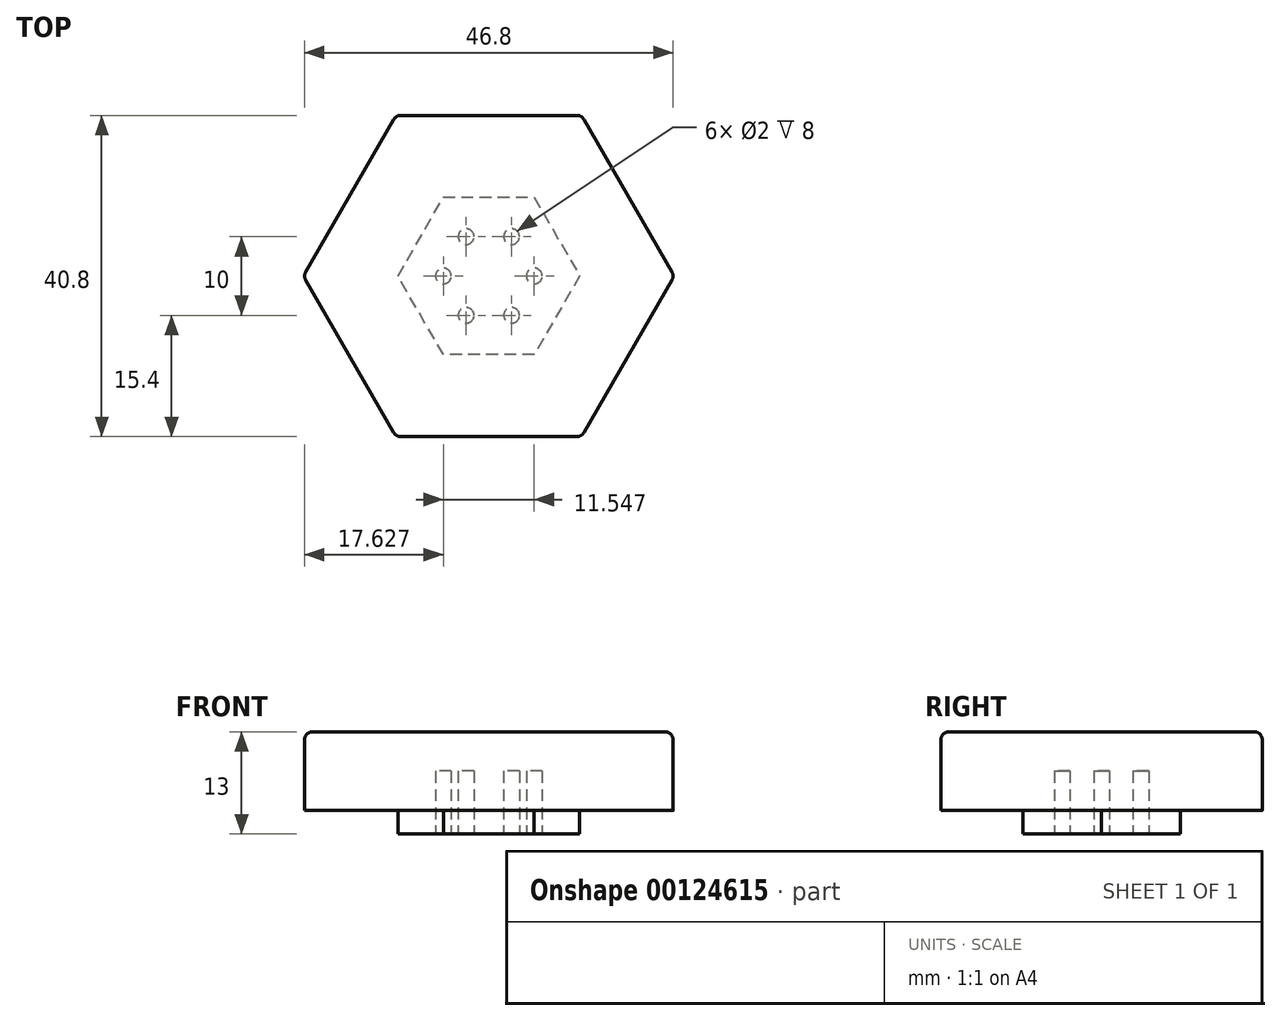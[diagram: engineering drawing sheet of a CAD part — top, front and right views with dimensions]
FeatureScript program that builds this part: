
annotation { "Feature Type Name" : "Feature", "Feature Type Description" : "" }
export const myFeature = defineFeature(function(context is Context, id is Id, definition is map)
    precondition{}
    {
        {
            var Q0;
            Q0=qCreatedBy(makeId("Top.planeOp"),FACE);
            var sketch = newSketch(context, id + "F0", { "sketchPlane" : qUnion([Q0])});
            skCircle(sketch, "E0.cCircle", {"center": v(0, 0) * mm, "radius": 10 * mm, "construction": true});
            skLineSegment(sketch, "E0.0", {"start": v(-5.77, 10) * mm, "end": v(5.77, 10) * mm});
            skLineSegment(sketch, "E0.1", {"start": v(5.77, 10) * mm, "end": v(11.55, 0) * mm});
            skLineSegment(sketch, "E0.2", {"start": v(11.55, 0) * mm, "end": v(5.77, -10) * mm});
            skLineSegment(sketch, "E0.3", {"start": v(5.77, -10) * mm, "end": v(-5.77, -10) * mm});
            skLineSegment(sketch, "E0.4", {"start": v(-5.77, -10) * mm, "end": v(-11.55, 0) * mm});
            skLineSegment(sketch, "E0.5", {"start": v(-11.55, 0) * mm, "end": v(-5.77, 10) * mm});
            skPoint(sketch, "E0.0.midPoint", {"position": v(0, 10) * mm});
            skLineSegment(sketch, "E1.0", {"start": v(-2.89, 5) * mm, "end": v(2.89, 5) * mm});
            skLineSegment(sketch, "E1.1", {"start": v(5.77, 0) * mm, "end": v(2.89, -5) * mm});
            skLineSegment(sketch, "E1.2", {"start": v(2.89, -5) * mm, "end": v(-2.89, -5) * mm});
            skLineSegment(sketch, "E1.3", {"start": v(2.89, 5) * mm, "end": v(5.77, 0) * mm});
            skLineSegment(sketch, "E1.4", {"start": v(-2.89, -5) * mm, "end": v(-5.77, 0) * mm});
            skLineSegment(sketch, "E1.5", {"start": v(-5.77, 0) * mm, "end": v(-2.89, 5) * mm});
            skCircle(sketch, "E2", {"center": v(2.89, 5) * mm, "radius": 1 * mm});
            skCircle(sketch, "E3.1.0", {"center": v(-2.89, 5) * mm, "radius": 1 * mm});
            skCircle(sketch, "E3.2.0", {"center": v(-5.77, 0) * mm, "radius": 1 * mm});
            skCircle(sketch, "E3.3.0", {"center": v(-2.89, -5) * mm, "radius": 1 * mm});
            skCircle(sketch, "E3.4.0", {"center": v(2.89, -5) * mm, "radius": 1 * mm});
            skCircle(sketch, "E3.5.0", {"center": v(5.77, 0) * mm, "radius": 1 * mm});
            skSolve(sketch);
        }
        {
            var Q0;
            Q0=makeQuery(id+"F0.imprint","IMPRINT",FACE,{"disambiguationData":[TD([[makeQuery(id+"F0.imprint","IMPRINT",EDGE,{"derivedFrom":sQuery(id+"F0.wireOp",EDGE,"E0.0")}),-1.0]])]});
            var Q1;
            Q1=makeQuery(id+"F0.imprint","IMPRINT",FACE,{"disambiguationData":[TD([[makeQuery(id+"F0.imprint","IMPRINT",EDGE,{"derivedFrom":sQuery(id+"F0.wireOp",EDGE,"E0.0")}),-1.0]])]});
            var Q2;
            {var subQ5=sQuery(id+"F0.wireOp",EDGE,"E3.1.0");var subQ6=sQuery(id+"F0.wireOp",EDGE,"E1.0");var subQ7=makeQuery(id+"F0.imprint","INTERSECT",VERTEX,{"derivedFrom":[subQ6,subQ5]});Q2=makeQuery(id+"F0.imprint","IMPRINT",FACE,{"disambiguationData":[TD([[makeQuery(id+"F0.imprint","IMPRINT",EDGE,{"disambiguationData":[TD([[subQ7,-1.0]])],"derivedFrom":subQ6}),-1.0]])]});}
            extrude(context, id + "F1", {"entities" : qUnion([Q0, Q1, Q2]), "depth" : 3 * mm});
        }
        {
            var Q0;
            Q0=makeQuery(id+"F1.opExtrude","CAP_FACE",FACE,{"disambiguationData":[OSD([sQuery(id+"F0.wireOp",EDGE,"E0.0"),sQuery(id+"F0.wireOp",EDGE,"E0.1"),sQuery(id+"F0.wireOp",EDGE,"E0.2"),sQuery(id+"F0.wireOp",EDGE,"E0.3"),sQuery(id+"F0.wireOp",EDGE,"E0.4"),sQuery(id+"F0.wireOp",EDGE,"E0.5")])],"isStart":false});
            var sketch = newSketch(context, id + "F2", { "sketchPlane" : qUnion([Q0])});
            skCircle(sketch, "E4.cCircle", {"center": v(0, 0) * mm, "radius": 20.4 * mm, "construction": true});
            skLineSegment(sketch, "E4.0", {"start": v(-11.78, 20.4) * mm, "end": v(11.78, 20.4) * mm});
            skLineSegment(sketch, "E4.1", {"start": v(11.78, 20.4) * mm, "end": v(23.56, 0) * mm});
            skLineSegment(sketch, "E4.2", {"start": v(23.56, 0) * mm, "end": v(11.78, -20.4) * mm});
            skLineSegment(sketch, "E4.3", {"start": v(11.78, -20.4) * mm, "end": v(-11.78, -20.4) * mm});
            skLineSegment(sketch, "E4.4", {"start": v(-11.78, -20.4) * mm, "end": v(-23.56, 0) * mm});
            skLineSegment(sketch, "E4.5", {"start": v(-23.56, 0) * mm, "end": v(-11.78, 20.4) * mm});
            skPoint(sketch, "E4.0.midPoint", {"position": v(0, 20.4) * mm});
            skSolve(sketch);
        }
        {
            var Q0;
            Q0=qSketchRegion(id+"F2",true);
            var Q1;
            Q1=makeQuery(id+"F2.imprint","IMPRINT",FACE,{"disambiguationData":[TD([[makeQuery(id+"F2.imprint","IMPRINT",EDGE,{"derivedFrom":sQuery(id+"F2.wireOp",EDGE,"E4.0")}),-1.0]])]});
            extrude(context, id + "F3", {"entities" : qUnion([Q0, Q1]), "operationType" : NewBodyOperationType.ADD, "depth" : 10 * mm});
        }
        {
            var Q0;
            Q0=makeQuery(id+"F3.opExtrude","CAP_EDGE",EDGE,{"disambiguationData":[OSD([sQuery(id+"F2.wireOp",EDGE,"E4.5")])],"isStart":false});
            var Q1;
            Q1=makeQuery(id+"F3.opExtrude","CAP_EDGE",EDGE,{"disambiguationData":[OSD([sQuery(id+"F2.wireOp",EDGE,"E4.4")])],"isStart":false});
            var Q2;
            Q2=makeQuery(id+"F3.opExtrude","CAP_EDGE",EDGE,{"disambiguationData":[OSD([sQuery(id+"F2.wireOp",EDGE,"E4.3")])],"isStart":false});
            var Q3;
            Q3=makeQuery(id+"F3.opExtrude","CAP_EDGE",EDGE,{"disambiguationData":[OSD([sQuery(id+"F2.wireOp",EDGE,"E4.2")])],"isStart":false});
            var Q4;
            Q4=makeQuery(id+"F3.opExtrude","CAP_EDGE",EDGE,{"disambiguationData":[OSD([sQuery(id+"F2.wireOp",EDGE,"E4.1")])],"isStart":false});
            var Q5;
            Q5=makeQuery(id+"F3.opExtrude","CAP_EDGE",EDGE,{"disambiguationData":[OSD([sQuery(id+"F2.wireOp",EDGE,"E4.0")])],"isStart":false});
            var Q6;
            Q6=makeQuery(id+"F3.opExtrude","SWEPT_EDGE",EDGE,{"disambiguationData":[OSD([sQuery(id+"F2.wireOp",EDGE,"E4.0"),sQuery(id+"F2.wireOp",EDGE,"E4.5")])]});
            var Q7;
            Q7=makeQuery(id+"F3.opExtrude","SWEPT_EDGE",EDGE,{"disambiguationData":[OSD([sQuery(id+"F2.wireOp",EDGE,"E4.0"),sQuery(id+"F2.wireOp",EDGE,"E4.1")])]});
            var Q8;
            Q8=makeQuery(id+"F3.opExtrude","SWEPT_EDGE",EDGE,{"disambiguationData":[OSD([sQuery(id+"F2.wireOp",EDGE,"E4.1"),sQuery(id+"F2.wireOp",EDGE,"E4.2")])]});
            var Q9;
            Q9=makeQuery(id+"F3.opExtrude","SWEPT_EDGE",EDGE,{"disambiguationData":[OSD([sQuery(id+"F2.wireOp",EDGE,"E4.4"),sQuery(id+"F2.wireOp",EDGE,"E4.5")])]});
            var Q10;
            Q10=makeQuery(id+"F3.opExtrude","SWEPT_EDGE",EDGE,{"disambiguationData":[OSD([sQuery(id+"F2.wireOp",EDGE,"E4.2"),sQuery(id+"F2.wireOp",EDGE,"E4.3")])]});
            var Q11;
            Q11=makeQuery(id+"F3.opExtrude","SWEPT_EDGE",EDGE,{"disambiguationData":[OSD([sQuery(id+"F2.wireOp",EDGE,"E4.3"),sQuery(id+"F2.wireOp",EDGE,"E4.4")])]});
            fillet(context, id + "F4", {"entities" : qUnion([Q0, Q1, Q2, Q3, Q4, Q5, Q6, Q7, Q8, Q9, Q10, Q11]), "radius" : 1 * mm, "tangentPropagation" : true, "allowEdgeOverflow" : false});
        }
        {
            var Q0;
            Q0=makeQuery(id+"F3.boolean.opBoolean","SPLIT",FACE,{"disambiguationData":[TD([makeQuery(id+"F1.opExtrude","SWEPT_FACE",FACE,{"disambiguationData":[OSD([sQuery(id+"F0.wireOp",EDGE,"E3.3.0")])]})])],"derivedFrom":makeQuery(id+"F3.opExtrude","CAP_FACE",FACE,{"disambiguationData":[OSD([sQuery(id+"F2.wireOp",EDGE,"E4.0"),sQuery(id+"F2.wireOp",EDGE,"E4.1"),sQuery(id+"F2.wireOp",EDGE,"E4.2"),sQuery(id+"F2.wireOp",EDGE,"E4.3"),sQuery(id+"F2.wireOp",EDGE,"E4.4"),sQuery(id+"F2.wireOp",EDGE,"E4.5")])],"isStart":true})});
            var Q1;
            Q1=makeQuery(id+"F3.boolean.opBoolean","SPLIT",FACE,{"disambiguationData":[TD([makeQuery(id+"F1.opExtrude","SWEPT_FACE",FACE,{"disambiguationData":[OSD([sQuery(id+"F0.wireOp",EDGE,"E3.4.0")])]})])],"derivedFrom":makeQuery(id+"F3.opExtrude","CAP_FACE",FACE,{"disambiguationData":[OSD([sQuery(id+"F2.wireOp",EDGE,"E4.0"),sQuery(id+"F2.wireOp",EDGE,"E4.1"),sQuery(id+"F2.wireOp",EDGE,"E4.2"),sQuery(id+"F2.wireOp",EDGE,"E4.3"),sQuery(id+"F2.wireOp",EDGE,"E4.4"),sQuery(id+"F2.wireOp",EDGE,"E4.5")])],"isStart":true})});
            var Q2;
            Q2=makeQuery(id+"F3.boolean.opBoolean","SPLIT",FACE,{"disambiguationData":[TD([makeQuery(id+"F1.opExtrude","SWEPT_FACE",FACE,{"disambiguationData":[OSD([sQuery(id+"F0.wireOp",EDGE,"E3.5.0")])]})])],"derivedFrom":makeQuery(id+"F3.opExtrude","CAP_FACE",FACE,{"disambiguationData":[OSD([sQuery(id+"F2.wireOp",EDGE,"E4.0"),sQuery(id+"F2.wireOp",EDGE,"E4.1"),sQuery(id+"F2.wireOp",EDGE,"E4.2"),sQuery(id+"F2.wireOp",EDGE,"E4.3"),sQuery(id+"F2.wireOp",EDGE,"E4.4"),sQuery(id+"F2.wireOp",EDGE,"E4.5")])],"isStart":true})});
            var Q3;
            Q3=makeQuery(id+"F3.boolean.opBoolean","SPLIT",FACE,{"disambiguationData":[TD([makeQuery(id+"F1.opExtrude","SWEPT_FACE",FACE,{"disambiguationData":[OSD([sQuery(id+"F0.wireOp",EDGE,"E2")])]})])],"derivedFrom":makeQuery(id+"F3.opExtrude","CAP_FACE",FACE,{"disambiguationData":[OSD([sQuery(id+"F2.wireOp",EDGE,"E4.0"),sQuery(id+"F2.wireOp",EDGE,"E4.1"),sQuery(id+"F2.wireOp",EDGE,"E4.2"),sQuery(id+"F2.wireOp",EDGE,"E4.3"),sQuery(id+"F2.wireOp",EDGE,"E4.4"),sQuery(id+"F2.wireOp",EDGE,"E4.5")])],"isStart":true})});
            var Q4;
            Q4=makeQuery(id+"F3.boolean.opBoolean","SPLIT",FACE,{"disambiguationData":[TD([makeQuery(id+"F1.opExtrude","SWEPT_FACE",FACE,{"disambiguationData":[OSD([sQuery(id+"F0.wireOp",EDGE,"E3.1.0")])]})])],"derivedFrom":makeQuery(id+"F3.opExtrude","CAP_FACE",FACE,{"disambiguationData":[OSD([sQuery(id+"F2.wireOp",EDGE,"E4.0"),sQuery(id+"F2.wireOp",EDGE,"E4.1"),sQuery(id+"F2.wireOp",EDGE,"E4.2"),sQuery(id+"F2.wireOp",EDGE,"E4.3"),sQuery(id+"F2.wireOp",EDGE,"E4.4"),sQuery(id+"F2.wireOp",EDGE,"E4.5")])],"isStart":true})});
            var Q5;
            Q5=makeQuery(id+"F3.boolean.opBoolean","SPLIT",FACE,{"disambiguationData":[TD([makeQuery(id+"F1.opExtrude","SWEPT_FACE",FACE,{"disambiguationData":[OSD([sQuery(id+"F0.wireOp",EDGE,"E3.2.0")])]})])],"derivedFrom":makeQuery(id+"F3.opExtrude","CAP_FACE",FACE,{"disambiguationData":[OSD([sQuery(id+"F2.wireOp",EDGE,"E4.0"),sQuery(id+"F2.wireOp",EDGE,"E4.1"),sQuery(id+"F2.wireOp",EDGE,"E4.2"),sQuery(id+"F2.wireOp",EDGE,"E4.3"),sQuery(id+"F2.wireOp",EDGE,"E4.4"),sQuery(id+"F2.wireOp",EDGE,"E4.5")])],"isStart":true})});
            extrude(context, id + "F5", {"entities" : qUnion([Q0, Q1, Q2, Q3, Q4, Q5]), "operationType" : NewBodyOperationType.REMOVE, "oppositeDirection" : true, "depth" : 5 * mm});
        }
    });
